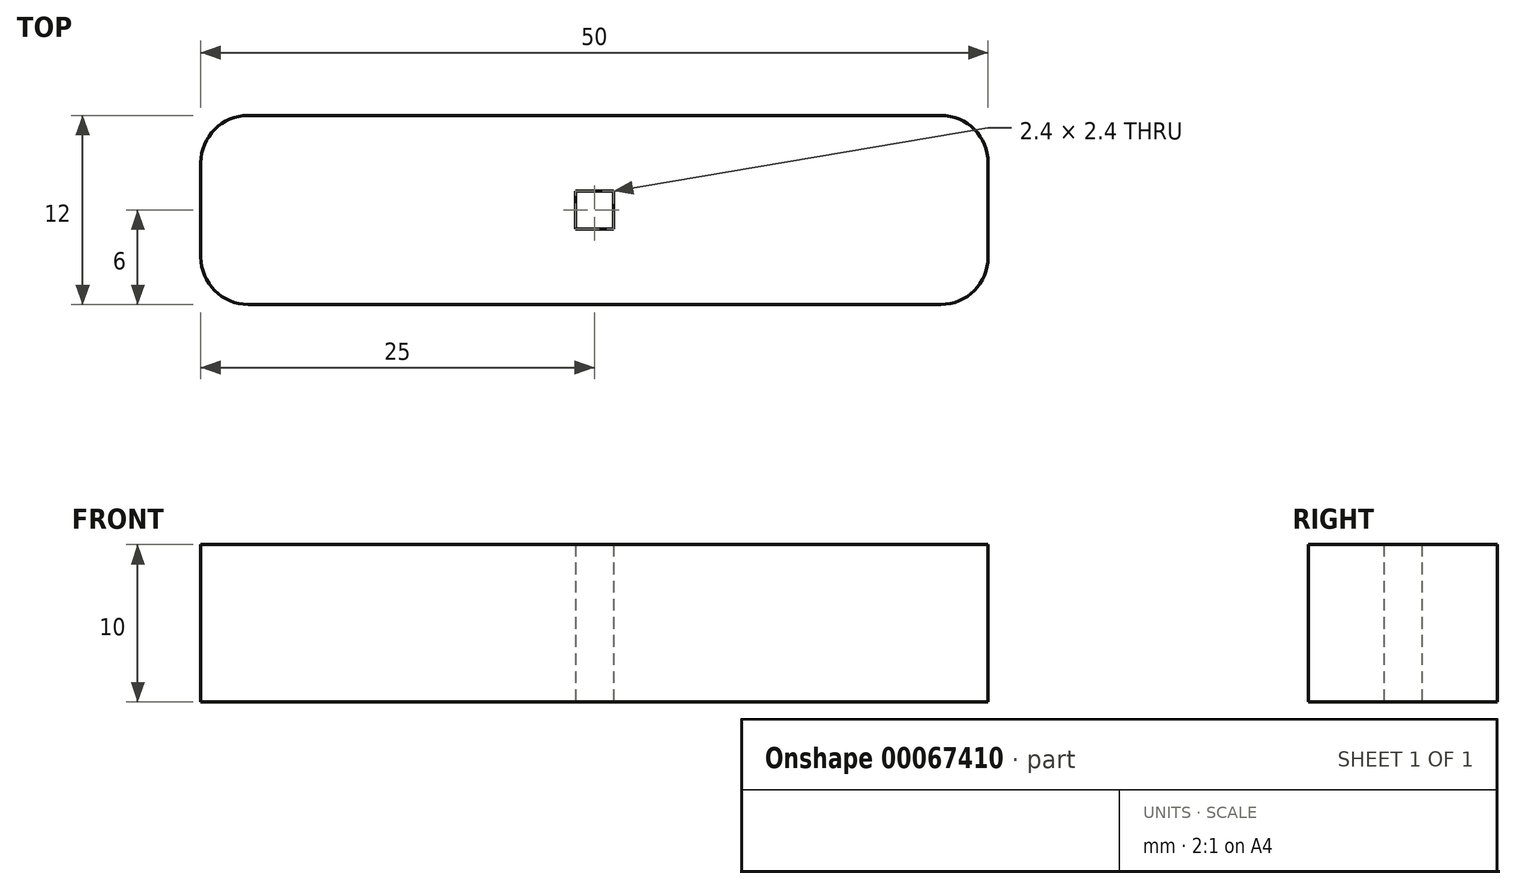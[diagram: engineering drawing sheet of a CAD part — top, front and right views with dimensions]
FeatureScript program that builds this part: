
annotation { "Feature Type Name" : "Feature", "Feature Type Description" : "" }
export const myFeature = defineFeature(function(context is Context, id is Id, definition is map)
    precondition{}
    {
        {
            var Q0;
            Q0=qCreatedBy(makeId("Top.planeOp"),FACE);
            var sketch = newSketch(context, id + "F0", { "sketchPlane" : qUnion([Q0])});
            skLineSegment(sketch, "E0.rect.bottom", {"start": v(-25, 6) * mm, "end": v(25, 6) * mm});
            skLineSegment(sketch, "E0.rect.top", {"start": v(-25, -6) * mm, "end": v(25, -6) * mm});
            skLineSegment(sketch, "E0.rect.left", {"start": v(-25, 6) * mm, "end": v(-25, -6) * mm});
            skLineSegment(sketch, "E0.rect.right", {"start": v(25, 6) * mm, "end": v(25, -6) * mm});
            skPoint(sketch, "E0.rect.middle", {"position": v(0, 0) * mm});
            skLineSegment(sketch, "E1.rect.bottom", {"start": v(-1.2, 1.2) * mm, "end": v(1.2, 1.2) * mm});
            skLineSegment(sketch, "E1.rect.top", {"start": v(-1.2, -1.2) * mm, "end": v(1.2, -1.2) * mm});
            skLineSegment(sketch, "E1.rect.left", {"start": v(-1.2, 1.2) * mm, "end": v(-1.2, -1.2) * mm});
            skLineSegment(sketch, "E1.rect.right", {"start": v(1.2, 1.2) * mm, "end": v(1.2, -1.2) * mm});
            skSolve(sketch);
        }
        {
            var Q0;
            Q0=makeQuery(id+"F0.imprint","IMPRINT",FACE,{"disambiguationData":[TD([[makeQuery(id+"F0.imprint","IMPRINT",EDGE,{"derivedFrom":sQuery(id+"F0.wireOp",EDGE,"E0.rect.bottom")}),-1.0]])]});
            extrude(context, id + "F1", {"entities" : qUnion([Q0]), "depth" : 10 * mm});
        }
        {
            var Q0;
            Q0=makeQuery(id+"F1.opExtrude","SWEPT_EDGE",EDGE,{"disambiguationData":[OSD([sQuery(id+"F0.wireOp",EDGE,"E0.rect.bottom"),sQuery(id+"F0.wireOp",EDGE,"E0.rect.left")])]});
            var Q1;
            Q1=makeQuery(id+"F1.opExtrude","SWEPT_EDGE",EDGE,{"disambiguationData":[OSD([sQuery(id+"F0.wireOp",EDGE,"E0.rect.top"),sQuery(id+"F0.wireOp",EDGE,"E0.rect.left")])]});
            var Q2;
            Q2=makeQuery(id+"F1.opExtrude","SWEPT_EDGE",EDGE,{"disambiguationData":[OSD([sQuery(id+"F0.wireOp",EDGE,"E0.rect.top"),sQuery(id+"F0.wireOp",EDGE,"E0.rect.right")])]});
            var Q3;
            Q3=makeQuery(id+"F1.opExtrude","SWEPT_EDGE",EDGE,{"disambiguationData":[OSD([sQuery(id+"F0.wireOp",EDGE,"E0.rect.bottom"),sQuery(id+"F0.wireOp",EDGE,"E0.rect.right")])]});
            fillet(context, id + "F2", {"entities" : qUnion([Q0, Q1, Q2, Q3]), "radius" : 3 * mm, "tangentPropagation" : true, "allowEdgeOverflow" : false});
        }
    });
